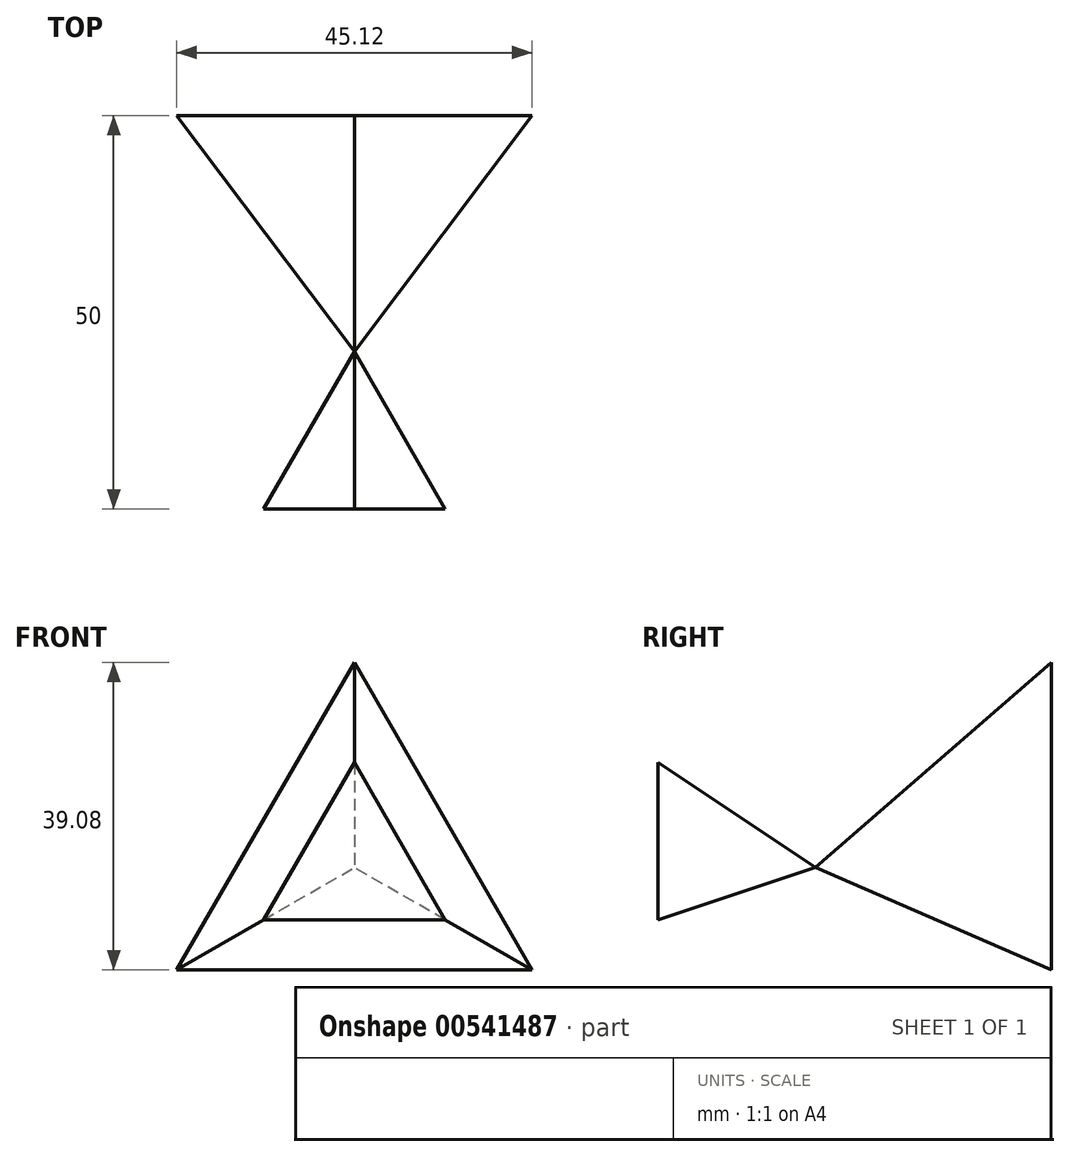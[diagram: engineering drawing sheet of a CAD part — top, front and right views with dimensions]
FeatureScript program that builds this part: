
annotation { "Feature Type Name" : "Feature", "Feature Type Description" : "" }
export const myFeature = defineFeature(function(context is Context, id is Id, definition is map)
    precondition{}
    {
        {
            var Q0;
            Q0=qCreatedBy(makeId("Front.planeOp"),FACE);
            var sketch = newSketch(context, id + "F0", { "sketchPlane" : qUnion([Q0])});
            skPoint(sketch, "E0", {"position": v(0, 0) * mm});
            skSolve(sketch);
        }
        {
            var Q0;
            Q0=qCreatedBy(makeId("Front.planeOp"),FACE);
            cPlane(context, id + "F1", {"entities" : qUnion([Q0]), "cplaneType" : CPlaneType.OFFSET, "offset" : 20 * mm, "width" : 152.4 * mm, "height" : 152.4 * mm});
        }
        {
            var Q0;
            Q0=qCreatedBy(id+"F1.planeOp",FACE);
            var sketch = newSketch(context, id + "F2", { "sketchPlane" : qUnion([Q0])});
            skCircle(sketch, "E1.cCircle", {"center": v(0, 0) * mm, "radius": 6.67 * mm, "construction": true});
            skLineSegment(sketch, "E1.0", {"start": v(11.55, -6.67) * mm, "end": v(-11.55, -6.67) * mm});
            skLineSegment(sketch, "E1.1", {"start": v(-11.55, -6.67) * mm, "end": v(0, 13.33) * mm});
            skLineSegment(sketch, "E1.2", {"start": v(0, 13.33) * mm, "end": v(11.55, -6.67) * mm});
            skPoint(sketch, "E1.0.midPoint", {"position": v(0, -6.67) * mm});
            skLineSegment(sketch, "E2", {"start": v(0, 13.33) * mm, "end": v(0, -6.67) * mm, "construction": true});
            skSolve(sketch);
        }
        {
            var Q0;
            Q0=qCreatedBy(makeId("Front.planeOp"),FACE);
            cPlane(context, id + "F3", {"entities" : qUnion([Q0]), "cplaneType" : CPlaneType.OFFSET, "offset" : 30 * mm, "oppositeDirection" : true, "width" : 152.4 * mm, "height" : 152.4 * mm});
        }
        {
            var Q0;
            Q0=qCreatedBy(id+"F3.planeOp",FACE);
            var sketch = newSketch(context, id + "F4", { "sketchPlane" : qUnion([Q0])});
            skCircle(sketch, "E3.cCircle", {"center": v(0, 0) * mm, "radius": 13.03 * mm, "construction": true});
            skLineSegment(sketch, "E3.0", {"start": v(0, 26.05) * mm, "end": v(22.56, -13.03) * mm});
            skLineSegment(sketch, "E3.1", {"start": v(22.56, -13.03) * mm, "end": v(-22.56, -13.03) * mm});
            skLineSegment(sketch, "E3.2", {"start": v(-22.56, -13.03) * mm, "end": v(0, 26.05) * mm});
            skPoint(sketch, "E3.0.midPoint", {"position": v(11.28, 6.51) * mm});
            skSolve(sketch);
        }
        {
            var Q0;
            Q0=makeQuery(id+"F2.imprint","IMPRINT",FACE,{"disambiguationData":[TD([[makeQuery(id+"F2.imprint","IMPRINT",EDGE,{"derivedFrom":sQuery(id+"F2.wireOp",EDGE,"E1.0")}),-1.0]])]});
            var Q1;
            Q1=sQuery(id+"F0.wireOp",VERTEX,"E0");
            loft(context, id + "F5", {"sheetProfilesArray" : [{ "sheetProfileEntities" : qUnion([Q0]) }, { "sheetProfileEntities" : qUnion([Q1]) }]});
        }
        {
            var Q0;
            Q0=makeQuery(id+"F4.imprint","IMPRINT",FACE,{"disambiguationData":[TD([[makeQuery(id+"F4.imprint","IMPRINT",EDGE,{"derivedFrom":sQuery(id+"F4.wireOp",EDGE,"E3.0")}),-1.0]])]});
            var Q1;
            Q1=qCreatedBy(makeId("Origin.pointOp"),VERTEX);
            loft(context, id + "F6", {"sheetProfilesArray" : [{ "sheetProfileEntities" : qUnion([Q0]) }, { "sheetProfileEntities" : qUnion([Q1]) }]});
        }
    });
